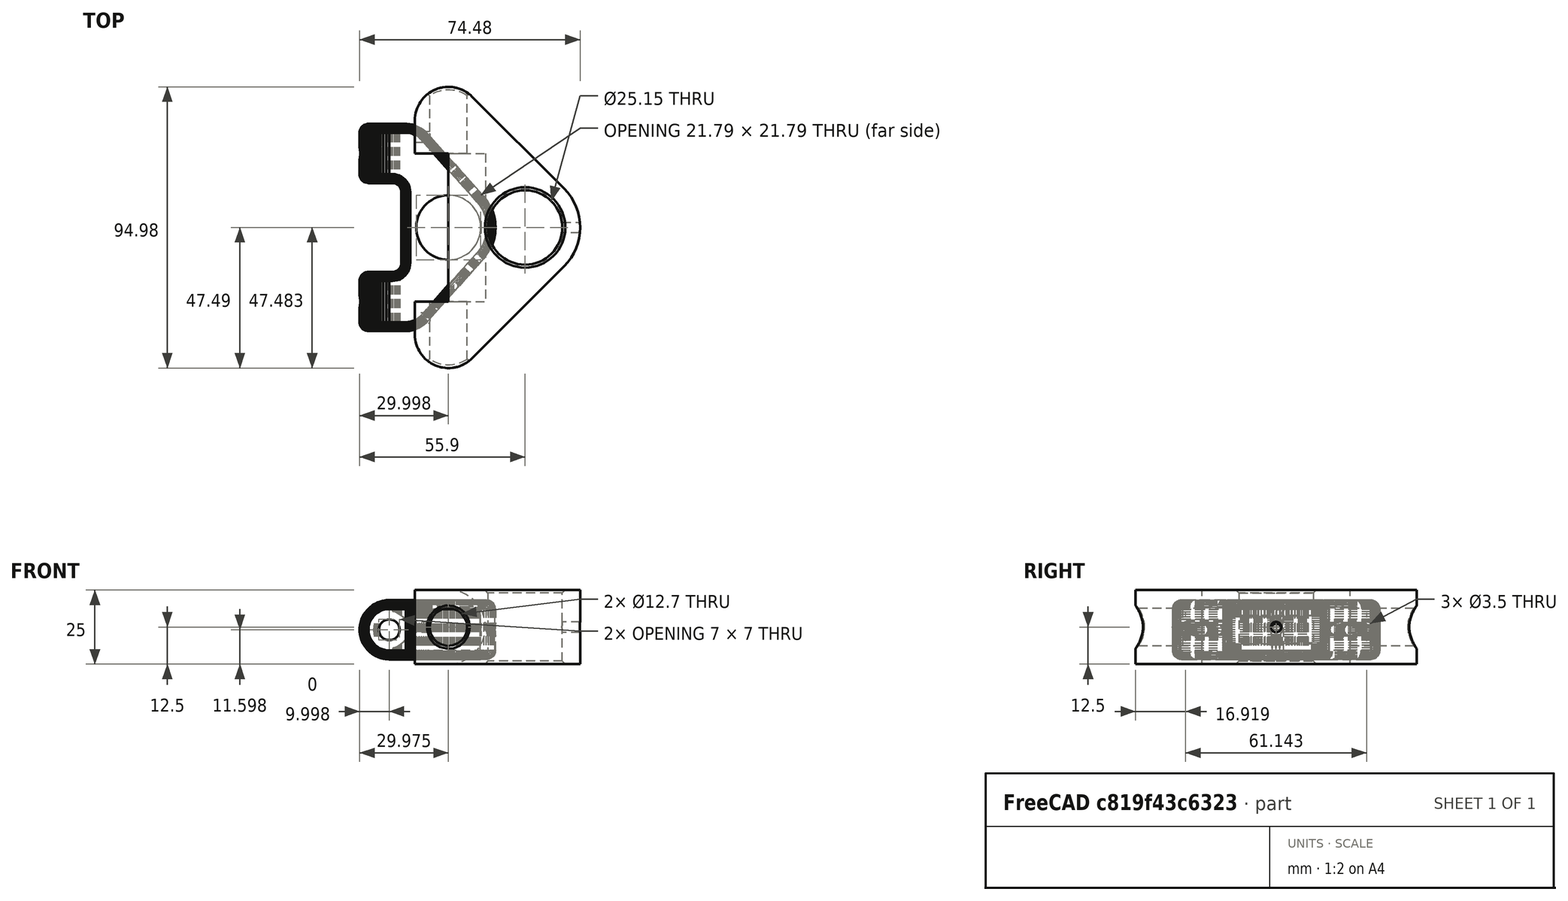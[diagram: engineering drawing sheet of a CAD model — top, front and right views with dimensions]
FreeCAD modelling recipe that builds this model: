
FCSTD DOCUMENT  (FreeCAD 2021.0301R23964 +3306 (Git))
Label: de_bracket
License: All rights reserved
objects: Sketcher::SketchObject×5, PartDesign::Pocket×4, Part::Feature×2, Mesh::Feature×1, Part::Refine×1, Spreadsheet::Sheet×1, PartDesign::Pad×1, PartDesign::Chamfer×1, PartDesign::Body×1
note: 27 computed .brp shape members not serialized (recipe doc carries the construction recipe); baked Part::Feature solids carry a one-line shape summary decoded from their .brp

FEATURE [Mesh::Feature] K1PDX_Yagi_Driven_Element_v1  label="K1PDX-Yagi-Driven-Element-v1"
FEATURE [Part::Feature] K1PDX_Yagi_Driven_Element_v1001
  shape: bbox 45.9 x 70 x 20 mm, 6746 faces, 0 solids (baked)
FEATURE [Part::Feature] K1PDX_Yagi_Driven_Element_v1001_solid  label="K1PDX_Yagi_Driven_Element_v1001 (Solid)"
  shape: bbox 45.9 x 70 x 20 mm, 6746 faces (baked)
FEATURE [Part::Refine] Refined  label="K1PDX_Yagi_Driven_Element_v1001 (Solid)001"
  Source = -> K1PDX_Yagi_Driven_Element_v1001_solid
FEATURE [Spreadsheet::Sheet] Spreadsheet  label="parameters"
  PythonMode = false
  cells = H1=NOTES; A2=boom hole diameter; B2(boom_dia)=25.15; C2=boom hole radius; D2(boom_rad)==boom_dia / 2; A3=boom hole thickness; B3(boom_thick)=6; A4=element hole diameter; B4(element_dia)=12.7; C4=element hole radius; D4(element_rad)==element_dia / 2; A5=element hole thickness; B5(element_thick)=5; A6=element cutout; B6(element_cutout)=50; A7=distance between boom and element; B7(b2e)=7; C7=cen2cen; D7(cen2cen)==boom_rad + element_rad + b2e; C8=relief to boom; D8(relief_thick)=0; E8=boom center to relief center; F8(relief2boom)==boom_dia + relief_thick; H8=I don't remember what these parameters were for; A9=body thickness; B9(body_thick)=25; A10=screw hole diameter; B10(screw_dia)=3.5; C10=screw hole radius; D10(screw_rad)==screw_dia / 2; A15==-45.9015 - -26.4449; A17=-36.7981; A18=-42.4015; A19==A18 - A17
FEATURE [Sketcher::SketchObject] Sketch
  FullyConstrained = true
  MapMode = 5
  Support = -> [XY_Plane]
  expr: Constraints[11] = <<parameters>>.boom_rad + <<parameters>>.boom_thick
  expr: Constraints[13] = <<parameters>>.element_rad + <<parameters>>.element_thick
  expr: Constraints[17] = <<parameters>>.element_rad + <<parameters>>.element_thick
  expr: Constraints[1] = <<parameters>>.boom_rad
  expr: Constraints[3] = <<parameters>>.element_rad
  expr: Constraints[4] = <<parameters>>.cen2cen
  sketch-geometry (8):
    g0: Circle CenterX=0 CenterY=0 CenterZ=0 NormalX=0 NormalY=0 NormalZ=1 AngleXU=0 Radius=12.575
    g1: Circle [constr] CenterX=-25.925 CenterY=0 CenterZ=0 NormalX=0 NormalY=0 NormalZ=1 AngleXU=0 Radius=6.35
    g2: LineSegment StartX=-17.8993 StartY=44.1684 StartZ=0 EndX=13.1345 EndY=13.1345 EndZ=0
    g3: LineSegment StartX=-17.8993 StartY=-44.1684 StartZ=0 EndX=13.1345 EndY=-13.1345 EndZ=0
    g4: ArcOfCircle CenterX=0 CenterY=0 CenterZ=0 NormalX=0 NormalY=0 NormalZ=1 AngleXU=0 Radius=18.575 StartAngle=5.49779 EndAngle=7.06858
    g5: LineSegment StartX=-37.275 StartY=36.1427 StartZ=0 EndX=-37.275 EndY=-36.1427 EndZ=0
    g6: ArcOfCircle CenterX=-25.925 CenterY=36.1427 CenterZ=0 NormalX=0 NormalY=0 NormalZ=1 AngleXU=0 Radius=11.35 StartAngle=0.785398 EndAngle=3.14159
    g7: ArcOfCircle CenterX=-25.925 CenterY=-36.1427 CenterZ=0 NormalX=0 NormalY=0 NormalZ=1 AngleXU=0 Radius=11.35 StartAngle=3.14159 EndAngle=5.49779
  constraints (21):
    c: Coincident(g0,g-1)
    c: Radius(g0) = 12.575
    c: PointOnObject(g1,g-1)
    c: Radius(g1) = 6.35
    c: DistanceX(g1,g0) = 25.925
    c: Angle(g2) = -0.785398
    c: Angle(g3) = 0.785398
    c: Equal(g3,g2)
    c: Symmetric(g2,g3,g-1)
    c: Coincident(g4,g0)
    c: Coincident(g4,g3)
    c: Radius(g4) = 18.575
    c: Tangent(g4,g2) = 1.5708
    c: DistanceX(g5,g1) = 11.35
    c: Symmetric(g5,g5,g-1)
    c: Tangent(g6,g2) = 1.5708
    c: Tangent(g6,g5) = -1.5708
    c: Radius(g6) = 11.35
    c: Coincident(g7,g5)
    c: Coincident(g7,g3)
    c: Equal(g7,g6)
FEATURE [PartDesign::Pad] Pad
  ClaimChildren = false
  Direction = (1,1,1)
  Fit = 0
  FitJoin = 0
  InnerFit = 0
  InnerFitJoin = 0
  InnerTaperAngle = 0
  InnerTaperAngleRev = 0
  Length = 25
  Length2 = 100
  Midplane = true
  NewSolid = false
  Profile = -> Sketch
  Suppress = false
  Type = 0
  UsePipeForDraft = true
  expr: Length = <<parameters>>.body_thick
FEATURE [Sketcher::SketchObject] Sketch001  label="element hole"
  FullyConstrained = true
  MapMode = 5
  Placement = pos=(0,0,0) rot=(1,0,0;1.5708rad)
  Support = -> [XZ_Plane]
  expr: Constraints[1] = <<parameters>>.element_rad
  expr: Constraints[2] = <<parameters>>.cen2cen
  sketch-geometry (1):
    g0: Circle CenterX=-25.925 CenterY=0 CenterZ=0 NormalX=0 NormalY=0 NormalZ=1 AngleXU=0 Radius=6.35
  constraints (3):
    c: PointOnObject(g0,g-1)
    c: Radius(g0) = 6.35
    c: DistanceX(g0,g-1) = 25.925
FEATURE [PartDesign::Pocket] Pocket
  BaseFeature = -> Pad
  ClaimChildren = false
  Fit = 0
  FitJoin = 0
  InnerFit = 0
  InnerFitJoin = 0
  InnerTaperAngle = 0
  InnerTaperAngleRev = 0
  Length = 200
  Length2 = 100
  Midplane = true
  NewSolid = false
  Profile = -> Sketch001
  Suppress = false
  Type = 0
  UsePipeForDraft = true
FEATURE [Sketcher::SketchObject] Sketch002
  FullyConstrained = true
  MapMode = 5
  Placement = pos=(0,0,0) rot=(1,0,0;1.5708rad)
  Support = -> [XZ_Plane]
  expr: Constraints[1] = <<parameters>>.cen2cen
  expr: Constraints[4] = <<parameters>>.body_thick / 2
  sketch-geometry (4):
    g0: ArcOfCircle CenterX=-25.925 CenterY=0 CenterZ=0 NormalX=0 NormalY=0 NormalZ=1 AngleXU=0 Radius=12.5 StartAngle=4.71239 EndAngle=7.85398
    g1: LineSegment StartX=-25.925 StartY=12.5 StartZ=0 EndX=-75.925 EndY=12.5 EndZ=0
    g2: LineSegment StartX=-75.925 StartY=12.5 StartZ=0 EndX=-75.925 EndY=-12.5 EndZ=0
    g3: LineSegment StartX=-75.925 StartY=-12.5 StartZ=0 EndX=-25.925 EndY=-12.5 EndZ=0
  constraints (12):
    c: PointOnObject(g0,g-1)
    c: DistanceX(g0,g-1) = 25.925
    c: Vertical(g0,g0)
    c: Vertical(g0,g0)
    c: Radius(g0) = 12.5
    c: Tangent(g0,g1) = -1.5708
    c: Coincident(g1,g2)
    c: Vertical(g2)
    c: Coincident(g2,g3)
    c: Coincident(g3,g0)
    c: Horizontal(g3)
    c: DistanceX(g1,g1) = 50
FEATURE [PartDesign::Pocket] Pocket001
  BaseFeature = -> Pocket
  ClaimChildren = false
  Fit = 0
  FitJoin = 0
  InnerFit = 0
  InnerFitJoin = 0
  InnerTaperAngle = 0
  InnerTaperAngleRev = 0
  Length = 50
  Length2 = 100
  Midplane = true
  NewSolid = false
  Profile = -> Sketch002
  Suppress = false
  Type = 0
  UsePipeForDraft = true
  expr: Length = <<parameters>>.element_cutout
FEATURE [Sketcher::SketchObject] Sketch004
  FullyConstrained = true
  MapMode = 5
  Placement = pos=(0,0,0) rot=(0.57735,0.57735,0.57735;2.0944rad)
  Support = -> [YZ_Plane]
  expr: Constraints[1] = <<parameters>>.screw_rad
  sketch-geometry (1):
    g0: Circle CenterX=0 CenterY=0 CenterZ=0 NormalX=0 NormalY=0 NormalZ=1 AngleXU=0 Radius=1.75
  constraints (2):
    c: Coincident(g0,g-1)
    c: Radius(g0) = 1.75
FEATURE [PartDesign::Pocket] Pocket002
  BaseFeature = -> Pocket001
  ClaimChildren = false
  Fit = 0
  FitJoin = 0
  InnerFit = 0
  InnerFitJoin = 0
  InnerTaperAngle = 0
  InnerTaperAngleRev = 0
  Length = 50
  Length2 = 100
  NewSolid = false
  Profile = -> Sketch004
  Reversed = true
  Suppress = false
  Type = 0
  UsePipeForDraft = true
FEATURE [Sketcher::SketchObject] Sketch005
  ExternalGeometry = -> [Pocket002]
  FullyConstrained = true
  MapMode = 5
  Placement = pos=(-37.275,0,0) rot=(0.57735,-0.57735,-0.57735;2.0944rad)
  Support = -> [Pocket002]
  expr: Constraints[2] = <<parameters>>.screw_rad
  sketch-geometry (6):
    g0: Circle CenterX=-30.5713 CenterY=0 CenterZ=0 NormalX=0 NormalY=0 NormalZ=1 AngleXU=0 Radius=1.75
    g1: Circle CenterX=30.5713 CenterY=0 CenterZ=0 NormalX=0 NormalY=0 NormalZ=1 AngleXU=0 Radius=1.75
    g2: LineSegment [constr] StartX=-36.1427 StartY=12.5 StartZ=0 EndX=-30.5713 EndY=0 EndZ=0
    g3: LineSegment [constr] StartX=-30.5713 StartY=0 StartZ=0 EndX=-25 EndY=-12.5 EndZ=0
    g4: LineSegment [constr] StartX=36.1427 StartY=12.5 StartZ=0 EndX=30.5713 EndY=0 EndZ=0
    g5: LineSegment [constr] StartX=30.5713 StartY=0 StartZ=0 EndX=25 EndY=-12.5 EndZ=0
  constraints (14):
    c: PointOnObject(g0,g-1)
    c: PointOnObject(g1,g-1)
    c: Radius(g0) = 1.75
    c: Equal(g0,g1)
    c: Coincident(g-6,g2)
    c: Coincident(g2,g0)
    c: Coincident(g2,g3)
    c: Coincident(g3,g-3)
    c: Equal(g3,g2)
    c: Coincident(g-5,g4)
    c: Coincident(g4,g1)
    c: Coincident(g4,g5)
    c: Coincident(g5,g-4)
    c: Equal(g5,g4)
FEATURE [PartDesign::Pocket] Pocket003
  BaseFeature = -> Pocket002
  ClaimChildren = false
  Fit = 0
  FitJoin = 0
  InnerFit = 0
  InnerFitJoin = 0
  InnerTaperAngle = 0
  InnerTaperAngleRev = 0
  Length = 6
  Length2 = 100
  NewSolid = false
  Profile = -> Sketch005
  Suppress = false
  Type = 0
  UsePipeForDraft = true
  expr: Length = <<parameters>>.boom_thick
FEATURE [PartDesign::Chamfer] Chamfer
  Angle = 45
  Base = -> Pocket003 [Edge30,Edge22,Edge42,Edge8]
  BaseFeature = -> Pocket003
  ChamferType = 0
  FlipDirection = false
  NewSolid = false
  Size = 1
  Size2 = 1
  SupportTransform = false
  Suppress = false
FEATURE [PartDesign::Body] Body
  AutoGroupSolids = false
  ExportMode = 0
  Group = -> [Sketch,Pad,Sketch001,Pocket,Sketch002,Pocket001,Sketch004,Pocket002,Sketch005,Pocket003,Chamfer]
  Origin = -> Origin
  Tip = -> Chamfer
  _ExportChildren = -> [Pad,Pocket,Pocket001,Pocket002,Pocket003,Chamfer]
  _GroupVersion = 1
